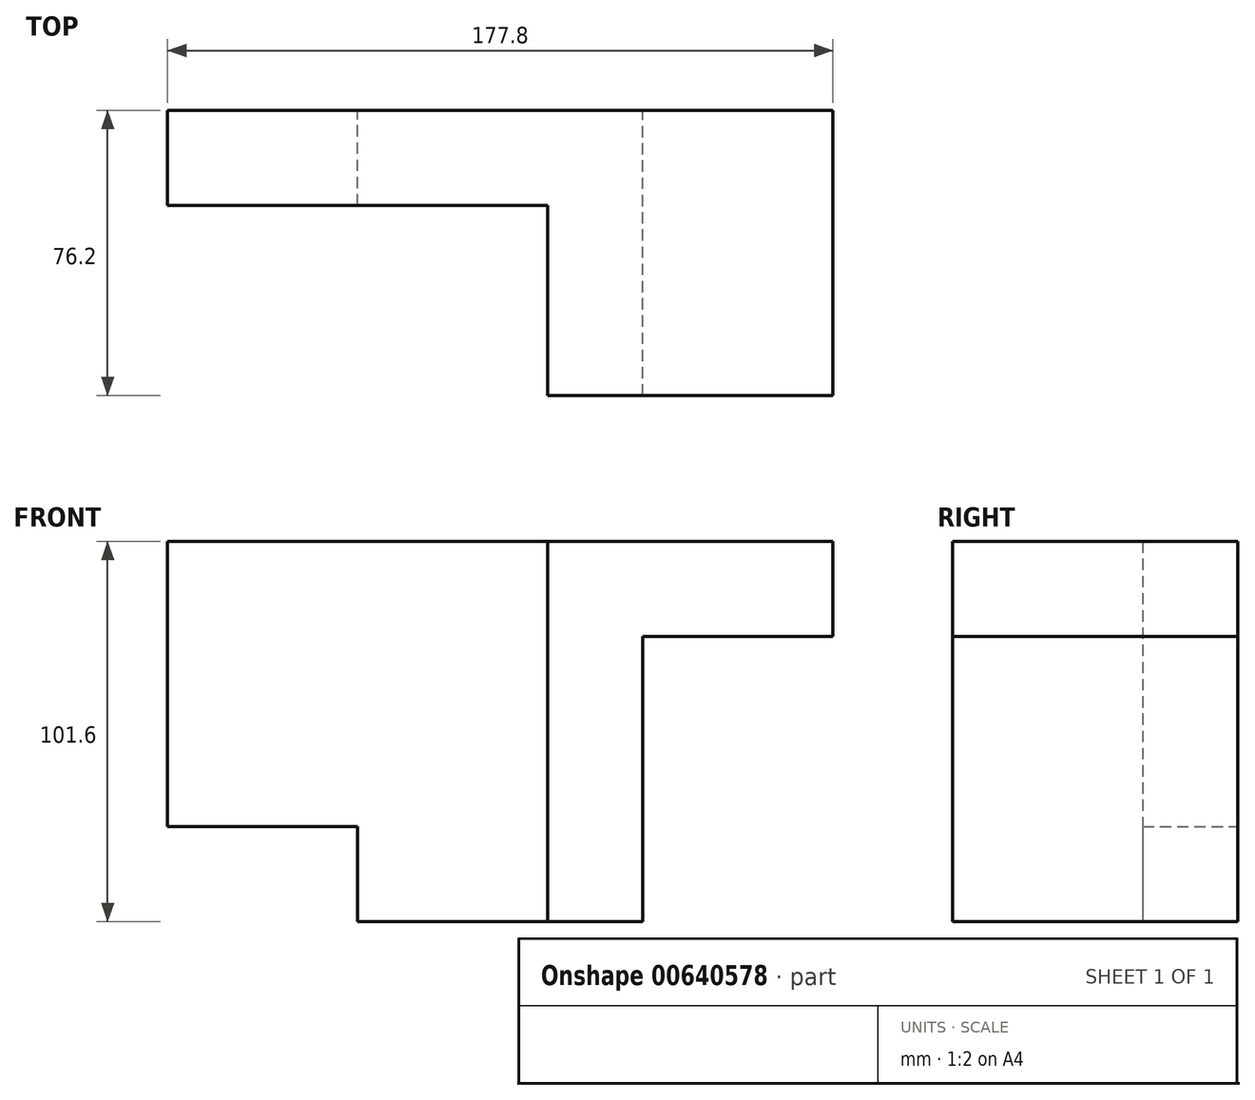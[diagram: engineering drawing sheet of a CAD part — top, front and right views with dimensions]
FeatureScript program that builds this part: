
annotation { "Feature Type Name" : "Feature", "Feature Type Description" : "" }
export const myFeature = defineFeature(function(context is Context, id is Id, definition is map)
    precondition{}
    {
        {
            var Q0;
            Q0=qCreatedBy(makeId("Front.planeOp"),FACE);
            var sketch = newSketch(context, id + "F0", { "sketchPlane" : qUnion([Q0])});
            skLineSegment(sketch, "E0.bottom", {"start": v(-22.9, 63.92) * mm, "end": v(53.3, 63.92) * mm});
            skLineSegment(sketch, "E0.top", {"start": v(-22.9, -37.68) * mm, "end": v(53.3, -37.68) * mm});
            skLineSegment(sketch, "E0.left", {"start": v(-22.9, 63.92) * mm, "end": v(-22.9, -37.68) * mm});
            skLineSegment(sketch, "E0.right", {"start": v(53.3, 63.92) * mm, "end": v(53.3, -37.68) * mm});
            skLineSegment(sketch, "E1.bottom", {"start": v(-22.9, 63.92) * mm, "end": v(-73.7, 63.92) * mm});
            skLineSegment(sketch, "E1.top", {"start": v(-22.9, -12.28) * mm, "end": v(-73.7, -12.28) * mm});
            skLineSegment(sketch, "E1.left", {"start": v(-22.9, 63.92) * mm, "end": v(-22.9, -12.28) * mm});
            skLineSegment(sketch, "E1.right", {"start": v(-73.7, 63.92) * mm, "end": v(-73.7, -12.28) * mm});
            skLineSegment(sketch, "E2.bottom", {"start": v(53.3, 63.92) * mm, "end": v(104.1, 63.92) * mm});
            skLineSegment(sketch, "E2.top", {"start": v(53.3, 38.52) * mm, "end": v(104.1, 38.52) * mm});
            skLineSegment(sketch, "E2.left", {"start": v(53.3, 63.92) * mm, "end": v(53.3, 38.52) * mm});
            skLineSegment(sketch, "E2.right", {"start": v(104.1, 63.92) * mm, "end": v(104.1, 38.52) * mm});
            skLineSegment(sketch, "E3", {"start": v(27.9, 63.92) * mm, "end": v(27.9, -37.68) * mm});
            skSolve(sketch);
        }
        {
            var Q0;
            Q0=makeQuery(id+"F0.imprint","IMPRINT",FACE,{"disambiguationData":[TD([[makeQuery(id+"F0.imprint","IMPRINT",EDGE,{"derivedFrom":sQuery(id+"F0.wireOp",EDGE,"E1.bottom")}),1.0]])]});
            var Q1;
            {var subQ1=sQuery(id+"F0.wireOp",EDGE,"E0.left");Q1=makeQuery(id+"F0.imprint","IMPRINT",FACE,{"disambiguationData":[TD([[makeQuery(id+"F0.imprint","IMPRINT",EDGE,{"derivedFrom":subQ1}),1.0]])]});}
            extrude(context, id + "F1", {"entities" : qUnion([Q0, Q1]), "depth" : 25.4 * mm, "offsetDistance" : 25.4 * mm});
        }
        {
            var Q0;
            {var subQ3=sQuery(id+"F0.wireOp",EDGE,"E0.right");Q0=makeQuery(id+"F0.imprint","IMPRINT",FACE,{"disambiguationData":[TD([[makeQuery(id+"F0.imprint","IMPRINT",EDGE,{"derivedFrom":subQ3}),-1.0]])]});}
            var Q1;
            Q1=makeQuery(id+"F0.imprint","IMPRINT",FACE,{"disambiguationData":[TD([[makeQuery(id+"F0.imprint","IMPRINT",EDGE,{"derivedFrom":sQuery(id+"F0.wireOp",EDGE,"E2.bottom")}),-1.0]])]});
            extrude(context, id + "F2", {"entities" : qUnion([Q0, Q1]), "operationType" : NewBodyOperationType.ADD, "depth" : 76.2 * mm, "offsetDistance" : 25.4 * mm});
        }
    });
